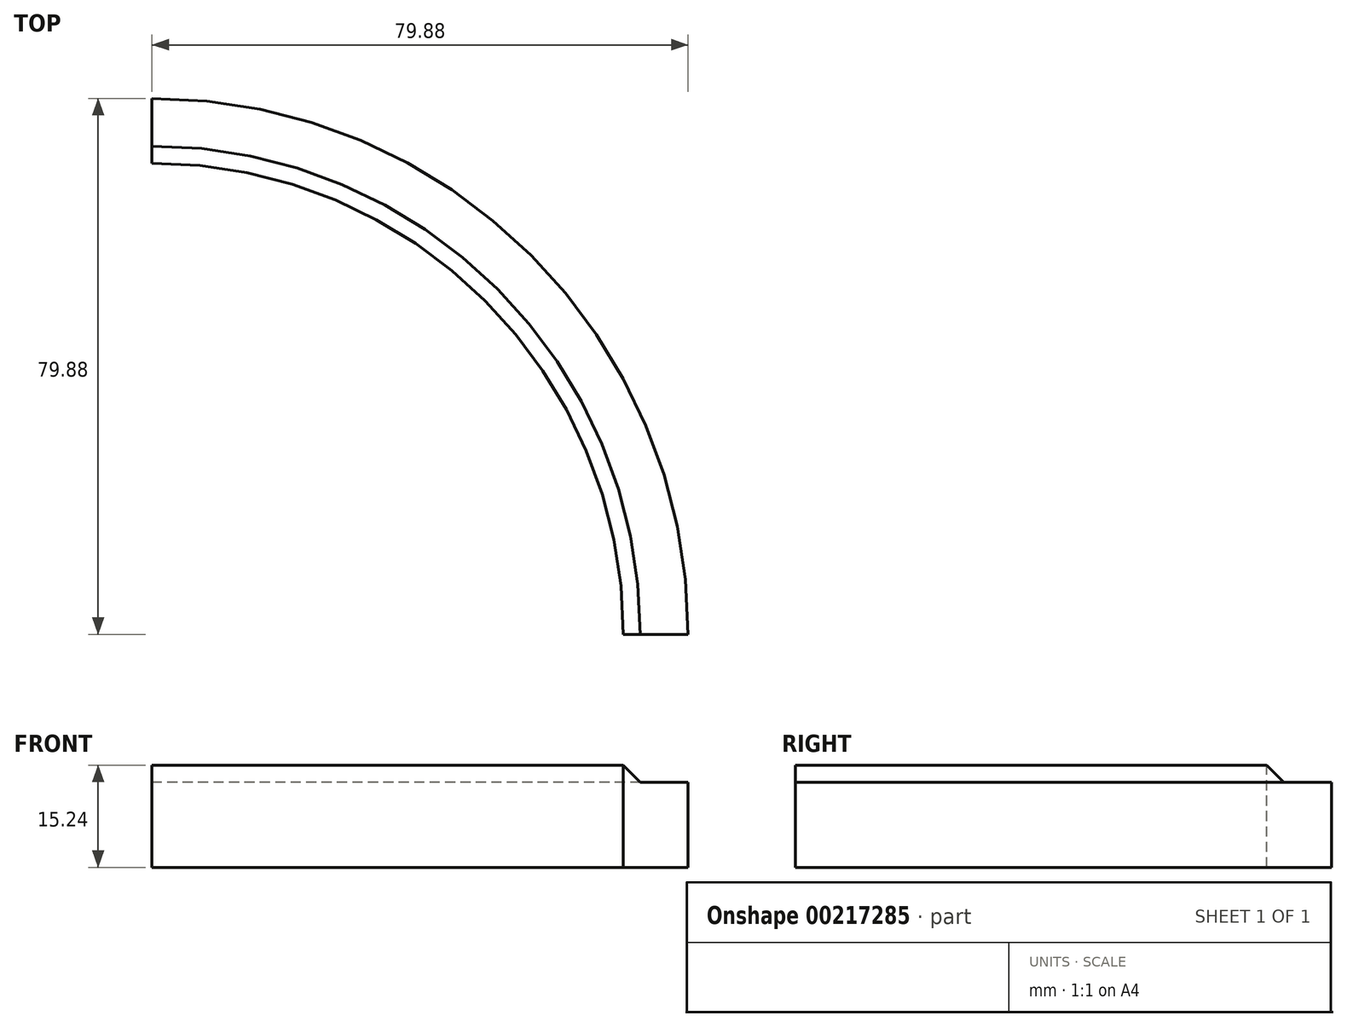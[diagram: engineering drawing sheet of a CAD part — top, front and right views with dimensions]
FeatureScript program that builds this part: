
annotation { "Feature Type Name" : "Feature", "Feature Type Description" : "" }
export const myFeature = defineFeature(function(context is Context, id is Id, definition is map)
    precondition{}
    {
        {
            var Q0;
            Q0=qCreatedBy(makeId("Right.planeOp"),FACE);
            var sketch = newSketch(context, id + "F0", { "sketchPlane" : qUnion([Q0])});
            skLineSegment(sketch, "E0", {"start": v(70.23, 0) * mm, "end": v(70.23, 15.24) * mm});
            skLineSegment(sketch, "E1", {"start": v(79.88, 12.7) * mm, "end": v(79.88, 0) * mm});
            skLineSegment(sketch, "E2", {"start": v(79.88, 0) * mm, "end": v(70.23, 0) * mm});
            skLineSegment(sketch, "E3", {"start": v(0, 56.17) * mm, "end": v(0, -44.6) * mm, "construction": true});
            skLineSegment(sketch, "E4", {"start": v(70.23, 15.24) * mm, "end": v(72.77, 12.7) * mm});
            skLineSegment(sketch, "E5", {"start": v(72.77, 12.7) * mm, "end": v(79.88, 12.7) * mm});
            skSolve(sketch);
        }
        {
            var Q0;
            Q0=qSketchRegion(id+"F0",true);
            var Q1;
            Q1=sQuery(id+"F0.wireOp",EDGE,"E3");
            revolve(context, id + "F1", {"entities" : qUnion([Q0]), "axis" : qUnion([Q1]), "revolveType" : RevolveType.ONE_DIRECTION, "angle" : 90 * degree});
        }
    });
